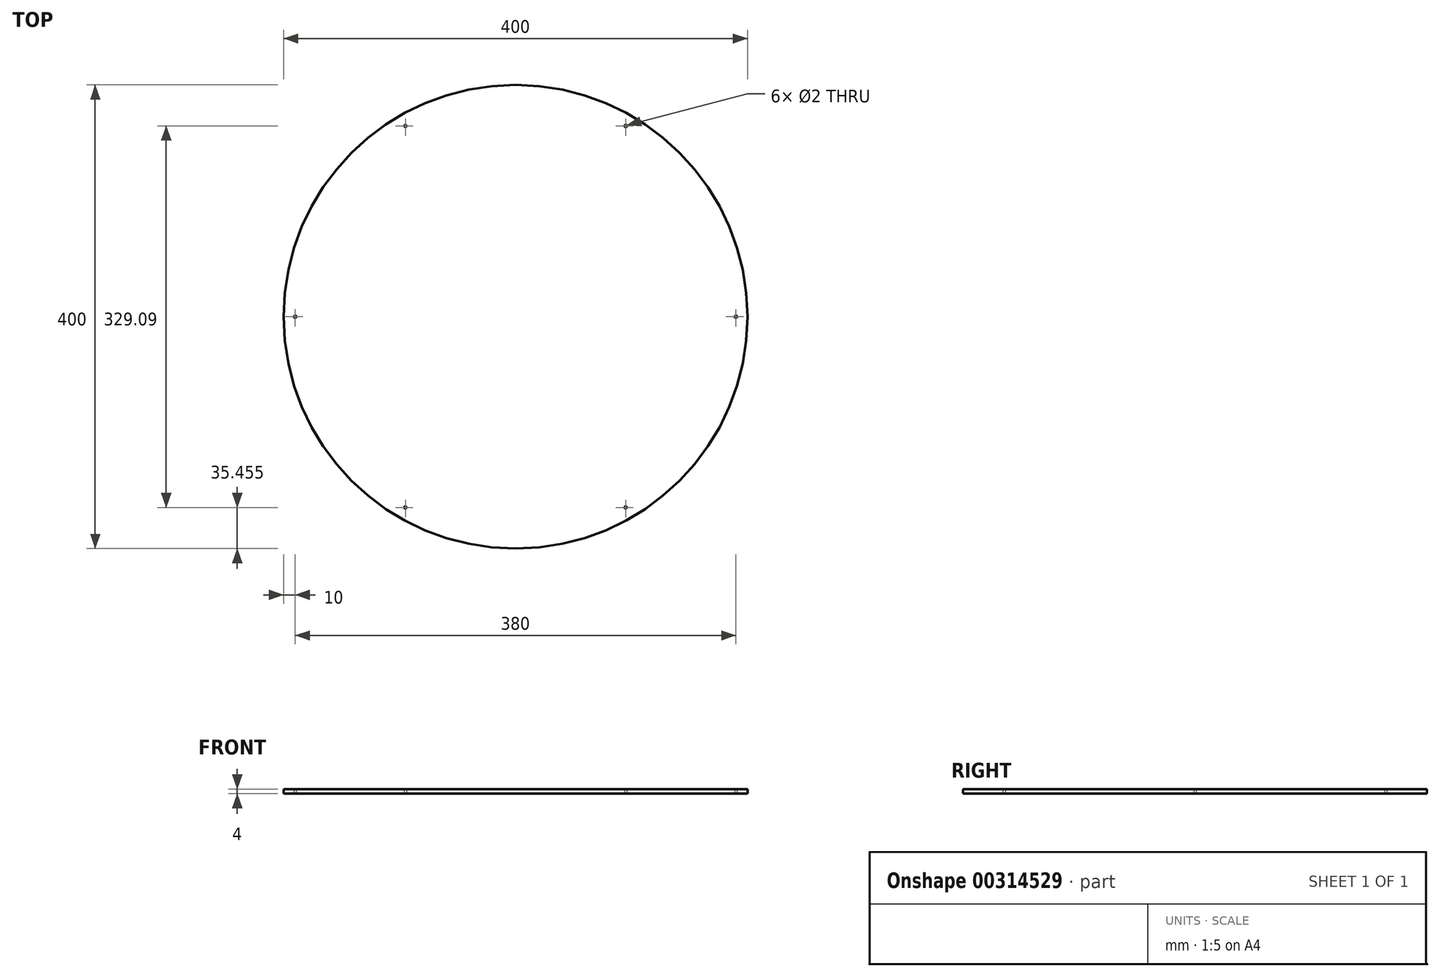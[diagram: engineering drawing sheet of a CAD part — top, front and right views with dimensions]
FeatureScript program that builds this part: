
annotation { "Feature Type Name" : "Feature", "Feature Type Description" : "" }
export const myFeature = defineFeature(function(context is Context, id is Id, definition is map)
    precondition{}
    {
        {
            var Q0;
            Q0=qCreatedBy(makeId("Top.planeOp"),FACE);
            var sketch = newSketch(context, id + "F0", { "sketchPlane" : qUnion([Q0])});
            skCircle(sketch, "E0", {"center": v(0, 0) * mm, "radius": 200 * mm});
            skCircle(sketch, "E1", {"center": v(-190, 0) * mm, "radius": 1 * mm});
            skCircle(sketch, "E2.1.0", {"center": v(-95, 164.54) * mm, "radius": 1 * mm});
            skCircle(sketch, "E2.2.0", {"center": v(95, 164.54) * mm, "radius": 1 * mm});
            skCircle(sketch, "E2.3.0", {"center": v(190, 0) * mm, "radius": 1 * mm});
            skCircle(sketch, "E2.4.0", {"center": v(95, -164.54) * mm, "radius": 1 * mm});
            skCircle(sketch, "E2.5.0", {"center": v(-95, -164.54) * mm, "radius": 1 * mm});
            skLineSegment(sketch, "E2.anchor1", {"start": v(0, 0) * mm, "end": v(-190, 0) * mm, "construction": true});
            skLineSegment(sketch, "E2.anchor2", {"start": v(0, 0) * mm, "end": v(-95, -164.54) * mm, "construction": true});
            skSolve(sketch);
        }
        {
            var Q0;
            Q0=makeQuery(id+"F0.imprint","IMPRINT",FACE,{"disambiguationData":[TD([[makeQuery(id+"F0.imprint","IMPRINT",EDGE,{"derivedFrom":sQuery(id+"F0.wireOp",EDGE,"E0")}),1.0]])]});
            extrude(context, id + "F1", {"entities" : qUnion([Q0]), "depth" : 4 * mm});
        }
    });
